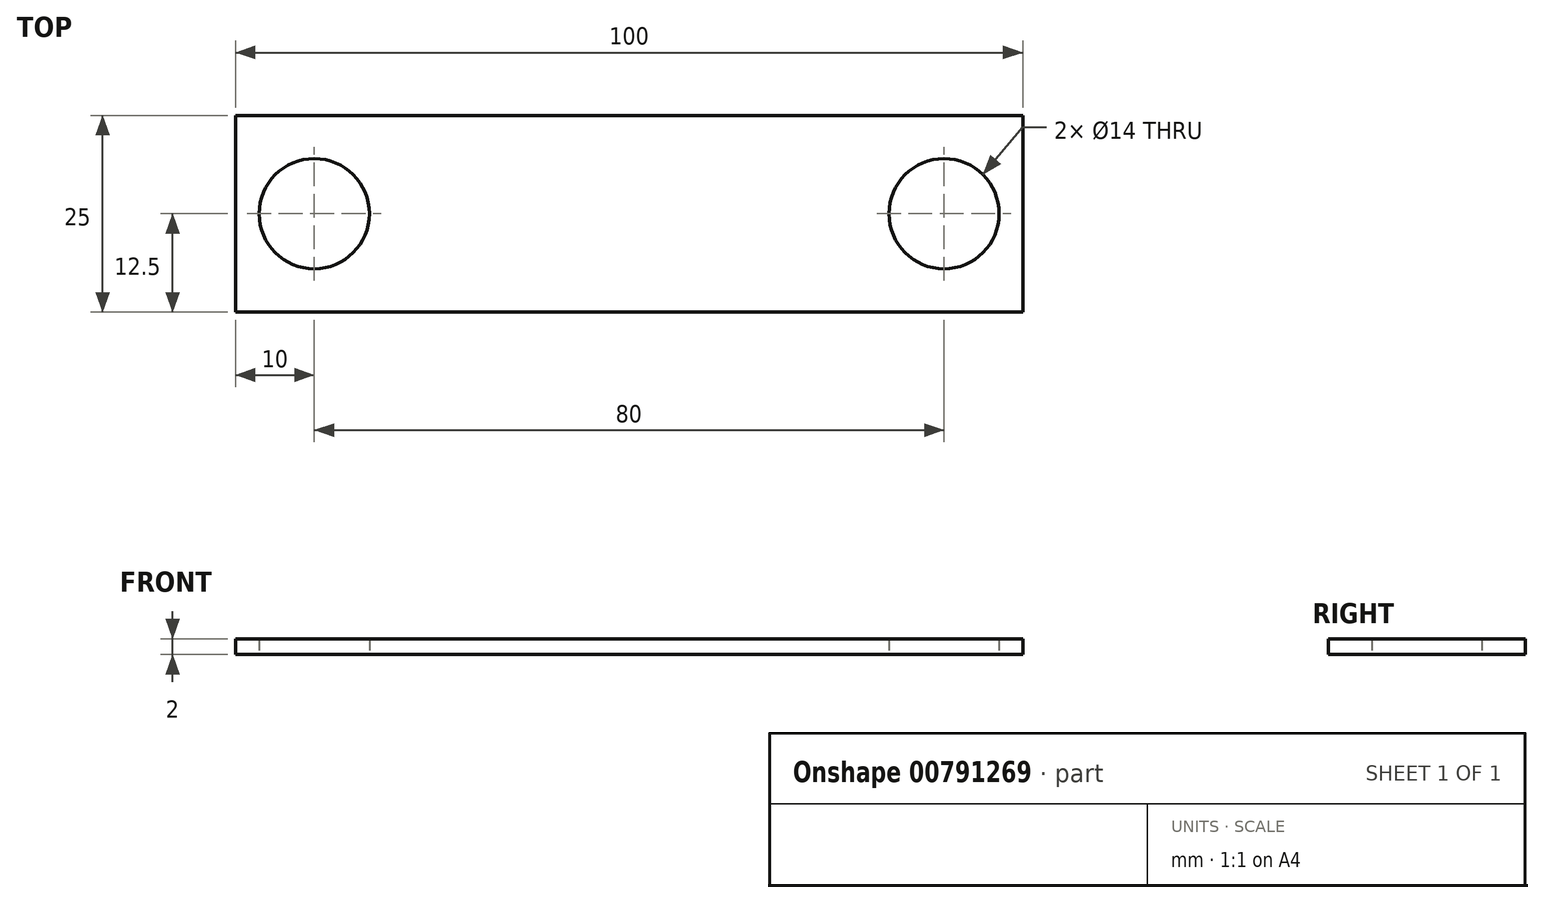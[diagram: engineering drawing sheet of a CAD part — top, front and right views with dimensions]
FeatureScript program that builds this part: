
annotation { "Feature Type Name" : "Feature", "Feature Type Description" : "" }
export const myFeature = defineFeature(function(context is Context, id is Id, definition is map)
    precondition{}
    {
        {
            var Q0;
            Q0=qCreatedBy(makeId("Top.planeOp"),FACE);
            var sketch = newSketch(context, id + "F0", { "sketchPlane" : qUnion([Q0])});
            skLineSegment(sketch, "E0", {"start": v(0, 0) * mm, "end": v(0, 25) * mm});
            skLineSegment(sketch, "E1", {"start": v(0, 25) * mm, "end": v(100, 25) * mm});
            skLineSegment(sketch, "E2", {"start": v(100, 25) * mm, "end": v(100, 0) * mm});
            skLineSegment(sketch, "E3", {"start": v(100, 0) * mm, "end": v(0, 0) * mm});
            skLineSegment(sketch, "E4", {"start": v(0, 0) * mm, "end": v(0, 12.5) * mm});
            skLineSegment(sketch, "E5", {"start": v(0, 12.5) * mm, "end": v(10, 12.5) * mm});
            skCircle(sketch, "E6", {"center": v(10, 12.5) * mm, "radius": 7 * mm});
            skLineSegment(sketch, "E7", {"start": v(100, 0) * mm, "end": v(100, 12.5) * mm});
            skLineSegment(sketch, "E8", {"start": v(100, 12.5) * mm, "end": v(90, 12.5) * mm});
            skCircle(sketch, "E9", {"center": v(90, 12.5) * mm, "radius": 7 * mm});
            skSolve(sketch);
        }
        {
            var Q0;
            Q0 = qSketchRegion(id + "F0", true);
            extrude(context, id + "F1", {"entities" : qUnion([Q0]), "depth" : 2 * mm, "offsetDistance" : 25 * mm});
        }
    });
